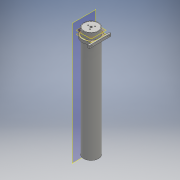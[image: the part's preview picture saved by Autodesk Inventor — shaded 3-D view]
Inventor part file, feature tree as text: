
AUTODESK INVENTOR PART (.ipt)
format: ipt  version: 2016 (Build 200138000, 138)  size: 618,496 bytes
history: native  units: mm
features: sketch x14, extrude x10, other x6, plane x5, pattern_circular x5, fillet x4, hole x4, revolve x2, mirror x1, projected_geometry x1
ambient origin geometry x8: Origin, YZ Plane, XZ Plane, XY Plane, X Axis, Y Axis, Z Axis, Center Point
bodies: Body1 (feature_tree), Body2 (feature_tree), Body3 (feature_tree), Body4 (feature_tree), Body5 (feature_tree)
feature tree (52):
  plane  "Work Plane1"
  other  "Work Axis1"
  revolve  "Revolution1"  [1 undecoded]
  extrude  "Extrusion3"  TaperAngle=90.0deg  [1 undecoded]
  fillet  "Fillet1"  [1 undecoded]
  plane  "Work Plane2"
  revolve  "Revolution2"  [1 undecoded]
  hole  "pipe thread inlet and outlet"  [1 undecoded]
  hole  "get it stuck"  [1 undecoded]
  extrude  "capture nut"  Depth=10.0mm
  pattern_circular  "Circular Pattern1"  [2 undecoded]
  pattern_circular  "Circular Pattern2"  [2 undecoded]
  extrude  "Extrusion5"  Depth=10.0mm TaperAngle=0.0deg
  plane  "Work Plane3"
  hole  "Hole3"  [1 undecoded]
  pattern_circular  "Circular Pattern3"  [2 undecoded]
  pattern_circular  "Circular Pattern4"  Angle=30.0deg  [1 undecoded]
  hole  "Hole4"  [1 undecoded]
  fillet  "Fillet2"  Radius=15.0mm
  plane  "Work Plane4"
  extrude  "Extrusion6"  Depth=10.0mm TaperAngle=360.0deg
  extrude  "Extrusion7"  Depth=10.0mm
  extrude  "Extrusion8"  Depth=10.0mm
  fillet  "Fillet4"  Radius=82.55mm
  mirror  "Mirror1"
  extrude  "Extrusion9"  Depth=10.0mm TaperAngle=0.0deg
  extrude  "extrude for drill template"  Depth=10.0mm TaperAngle=360.0deg
  extrude  "drill  template side wall"  Depth=10.0mm TaperAngle=360.0deg
  plane  "Work Plane5"
  extrude  "hole in holders"  Depth=10.0mm
  pattern_circular  "Circular Pattern5"  [2 undecoded]
  fillet  "Fillet3"  Radius=1.5875mm
  sketch  "Sketch3"  dims[d9=10.0mm d10=11.5mm]
  other  "inner"
  sketch  "Sketch4"  dims[d11=76.9mm d14=90.0deg d15=120.0deg]
  sketch  "Sketch5"  dims[d16=120.0deg d17=9.0mm]
  other  "cap"
  sketch  "Sketch6"  dims[d18=9.0mm d19=9.0mm]
  projected_geometry  "Projected Loop1"
  sketch  "Sketch7"  dims[d20=3.0mm d21=43.0mm]
  sketch  "Sketch8"  dims[d22=10.0mm d23=0.0mm d24=6.0mm]
  other  "tube"
  sketch  "Sketch9"  dims[d25=2.0mm]
  sketch  "Sketch10"  dims[d26=5.0mm]
  other  "mount"
  sketch  "Sketch11"  dims[d29=76.2mm]
  sketch  "Sketch12"  dims[d30=7.1882mm]
  sketch  "Sketch13"  dims[d31=16.0mm]
  sketch  "Sketch14"  dims[d32=90.0deg]
  other  "inner_cap_drill_template"
  sketch  "Sketch15"  dims[d144=10.0mm d145=10.0mm d35=11.1125mm d36=10.02mm d37=0.624793mm d38=10.732mm d39=4.0mm d40=2.0mm d41=90.0deg d42=17.076mm d43=20.594885mm]
  sketch  "Sketch16"  dims[d46=0.0mm d47=2.2mm d51=3.2mm d52=6.0mm d53=5.5mm d54=2.3mm d55=90.0deg d56=8.8mm d57=20.594885mm d58=13.95mm d59=5.8mm d60=2.5mm d61=0.0mm d64=30.0mm d65=360.0deg d67=16.0mm d68=30.0deg d69=30.0mm d70=360.0deg d72=15.0mm d73=30.0mm d75=360.0deg d77=16.764mm d78=76.2mm d79=82.55mm d80=609.6mm d81=0.0mm d82=2.6416mm d83=6.0mm d84=5.5mm d85=3.0mm d86=90.0deg d87=12.0mm d88=20.594885mm d89=30.0mm d90=360.0deg d92=30.0mm d93=360.0deg d95=24.1046mm d96=8.0mm d146=10.0mm d147=10.0mm d99=11.1125mm d100=8.608mm d101=0.624793mm d102=10.821mm d103=4.0mm d104=2.0mm d105=90.0deg d106=15.664mm d107=20.594885mm d112=1.5875mm d113=-35.0mm d115=8.0mm d116=60.0mm d117=8.0mm d118=3.175mm d119=20.0mm d120=7.5mm d121=15.0mm d122=0.0mm d123=2.0mm d124=4.0mm d126=3.2mm d127=8.0mm d128=8.0mm d129=8.0mm d130=0.0mm d131=1.5mm d132=6.0mm d133=3.2mm d134=8.0mm d135=0.0mm d136=5.5mm d137=2.3mm d138=0.0mm d142=41.5mm d143=69.342mm d148=4.0mm d149=0.6mm d150=0.4mm d151=0.4mm d152=0.0mm d153=0.4mm d154=12.0mm d155=0.0mm d156=1.0mm d157=15.0mm d158=0.0mm d159=30.0mm d160=360.0deg]
note: 17 required parameter values undecoded (feature->parameter linkage not recoverable at this tier; creation-order binding heuristic only, values carry confidence <= 0.55)